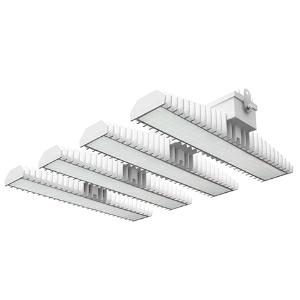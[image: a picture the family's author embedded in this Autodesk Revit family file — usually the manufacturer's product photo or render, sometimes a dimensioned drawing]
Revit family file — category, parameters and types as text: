
# Revit family: 3f_filippi_-_3f_lem_ho_ampio_3f_filippi_-_58974_a0812_-_3f_lem_4_ho_led_280_dali_cr_ampio___vs_b05d
name_source: partatom
category: Lighting Fixtures
units: mm (PartAtom-declared; Revit-internal decimal feet)

## family parameters
Cut with Voids When Loaded = No
Host = Face
Light Source = No
Part Type = Normal
Room Calculation Point = No
Round Connector Dimension = Use Diameter
Shared = No

## types (1)
- 3F Filippi - 3F LEM HO Ampio (1 x LED, 35405 lm, 276 W, 4000 K)
    Apparent Load = 276 VA
    Approval mark = CE
    CIE Flux Codes = 67 90 97 100 100
    Color Rendering = 80
    Color Temperature = 4000 K
    Control Gear = Electronic transformer
    Default Elevation = 1800 mm
    Description = Industrial luminaire with high light output and high luminous efficiency designed with the most innovative technologies for environments with temperature up to 55°C.

ILLUMINOTECHNICAL
Luminous efficiency 100% (DLOR 98%, ULOR 2%).
Initial luminous flux of the luminaire 35405 lm.
Direct symmetric wide distribution: the illuminated area has a rectangular shape.
Installation Interdistance Transv.D = 1.24 x hu - Long.D = 1.20 x hu.
Tabular UGR (CIE 117 - 4H-8H; S=0.25H; 70/50/20): RUG 23.8 - 23.9.
Beam angle: 82° - 83°.
Luminous efficacy 128 lm/W.
Lifetime (L93/B10): 30000 h. (tq+25°C)
Lifetime (L90/B10): 50000 h. (tq+25°C)
Lifetime (L85/B10): 80000 h. (tq+25°C)
Lifetime (L80/B10): 100000 h. (tq+25°C)
Lifetime (L85/B10): 50000 h. (tq+55°C)
Sudden decreased luminous flux after 50000 hours: 0% (C0).
Photobiological safety in compliance with IEC/TR 62778: RG0 risk exempt, (IEC 62471).
In compliance with IEC/EN 62722-2-1 - IEC/EN 62717 standards.

SOURCE
4 Mid-Power linear LED modules 70W/840.
Energy efficiency class (UE 2019/2020 - UE 2019/2015): C.
CIE 13.3 Colour rendering index: CRI >80 (R9 <50%).
IES TM-30 Fidelity Index: Rf = 84 Rg = 95.
CCT nominal colour temperature 4000 K.
Colour initial tolerance (MacAdam): SDCM 3.

MECHANICAL
Passive modular heatsinks in die-casted aluminium, painted in white colour.
To optimize the thermal management of the LED module, the heatsinks are oversized and provided with self-cleaning of cooling fins.
Wiring body in aluminium and galvanised steel anchored solidly to the sinks and thermally separated.
3F Lens lenses with high luminous efficiency, transparent methacrylate (PMMA), fixed to the LED modules.
Fixing brackets in stainless steel.
Luminaire with limited surface temperature. - D - (EN 60598-2-24)
Dimensions: 757x542 mm, height 133 mm. Weight 19.23 kg.
IP65 protection degree.
Mechanical strength to impacts IK06 (1 joule).
Glow-wire test resistance 650°C.

ELECTRICAL
Halogen Free DALI-2 DATI (Parts 251, 252, 253), PUSH-DIM, electronic wiring 230V-50/60Hz, power factor 0.97 at full load, THD <25%, constant output current, class I, 2 driver, 2 DALI addresses.
Power of the luminaire 276 W.
ENEC - CE.
SAFE FLICKER: PstLM=<1 and SVM=<0.4 (IEC TR 61547-1 and IEC TR 63158), to ensure a more comfortable and safe light.
Luminaire compliant with EN 60598-2-22 for power supply from a centralised emergency system CPSS (Central Power Supply System), not incorporated in the luminaire - high risk areas excluded. The default power and flux are 100% in AC and 15% in DC.
Ambient temperature from -30°C to +55°C.
Temperature class T6 max 85°C.
Quick connection via M25 5P connector with 9-13 mm tightening range.
Power unit positioned on a separate compartment by the LED module to ensure optimum temperatures of cabling components, to be inspectable and maintainable.
Relative humidity UR: <85%.

INSTALLATION
Ceiling / Suspended / Wall.
All accessories dedicated to this product are available on the Catalog and on our website www.3F-Filippi.com.

ACCESSORIES
A0812 - Anti-glare microprismatic VS moulded glass, tempered, not flammable, with sealing gasket.
One required for each light module. The pack contains 10 pieces.

APPLICATIONS
In commercial environments, exhibition and industrial areas, stores, open areas.
Environments in which it is necessary a total protection against falling fragments (eg environments with foodstuffs or machines with moving parts or with extreme temperature changes), use luminaires with polycarbonate lenses.

LIGHT MANAGEMENT
Recommended minimum setting: 10%.
The luminaire, equipped with (DALI-2 DATI) driver, can be controlled manually with 3F Easy Dim technology or automatically/manually with wired or wireless DALI/D2D control systems.
The D2D driver guarantees interoperability with other devices with the same certification by making the following information available:
Device Data (Part 251), Energy Report (Part 252), Diagnosis & Maintenance (Part 253).
In electrical systems without a regulation system (manual or automatic) and DALI bus, a suitable jumper must be made on the DA-DA terminals of the appliance.

WARNING
Fixture not suitable for cold stores with an ambient temperature <0°C and/or relative humidity >85%.
Luminaire designed for disposal/recycling at end-of-life.
Replaceable (LED only) light source by a professional. Replaceable control gear by a professional.
    Height = 133 mm  [stored 0.436352 ft]
    Lamp = 1 x LED
    Lamp Light Flux = 35405 lm
    Lamp Power = 276 W
    Lamp count = 1
    Length = 757 mm
    Lifetime = 50000 h
    Luminous efficacy = 128 lm/W
    Manufacturer = 3F Filippi
    ModVariant = No
    Model = 3F Filippi - 58974+A0812 - 3F LEM 4 HO LED 280 DALI CR AMPIO + VS
    Mounting Place = Ceiling
    Mounting Type = Pendant
    Number of Poles = 1
    OnlyDefault = Yes
    Power Factor = 1
    Product Name = 3F Filippi - 3F LEM HO Ampio
    Product group = pendant luminaire
    ProductGroupID = 9
    Protection Class = Protection class I
    Protection Degree = IP 65
    RLX_Detail_Level = 1
    RLX_Emergency_Light_Flux = 0 lm
    RLX_Emergency_Type = 0
    RLX_Emergency_Type_DB = No
    RlxData = <blob elided: 122405 chars, md5=27e9232e>
    Socket = socket
    Standby Power = 0 W
    System Light Flux = 35405 lm
    System Power = 276 W
    Type Comments = Product without accessories
    Type Image = 3f_filippi_-_lem_4__a0812.jpg
    URL = http://relux.com
    VarID = ---
    Voltage = 0 V
    Weight = 0.00 kg
    Width = 542 mm

note: [stored X ft] marks values corroborated as IEEE doubles in the binary element streams (Revit-internal decimal feet)

## geometry (parser evidence)
native form markers: Blend x4, Sweep x12
no freeform markers — native parametric forms only
